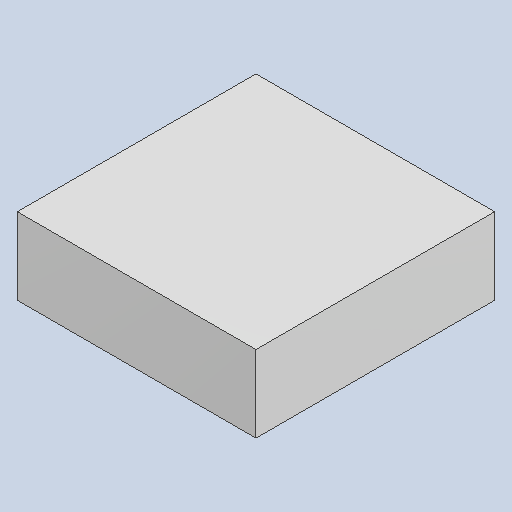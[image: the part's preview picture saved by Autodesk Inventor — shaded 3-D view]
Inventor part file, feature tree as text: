
AUTODESK INVENTOR PART (.ipt)
format: ipt  version: 2023.4 (Build 274418000, 418)  size: 79,872 bytes
history: native  units: mm
features: extrude x1
ambient origin geometry x8: Origin, YZ Plane, XZ Plane, XY Plane, X Axis, Y Axis, Z Axis, Center Point
bodies: Solid1 (feature_tree)
feature tree (1):
  extrude  "Extruded_1"  [1 undecoded]
note: 1 required parameter value undecoded (feature->parameter linkage not recoverable at this tier; creation-order binding heuristic only, values carry confidence <= 0.55)
